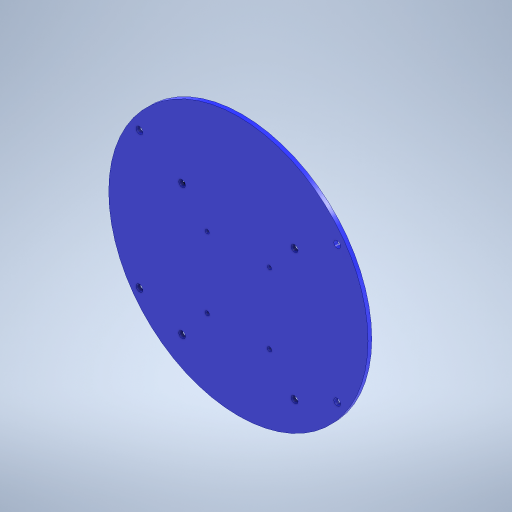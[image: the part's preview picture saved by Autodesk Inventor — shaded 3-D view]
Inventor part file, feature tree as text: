
AUTODESK INVENTOR PART (.ipt)
format: ipt  version: 2023 (Build 270158000, 158)  size: 334,848 bytes
history: native  units: mm
features: extrude x9, other x7, sketch x3, mirror x3, projected_geometry x1
ambient origin geometry x8: Origin, YZ Plane, XZ Plane, XY Plane, X Axis, Y Axis, Z Axis, Center Point
bodies: Body1 (feature_tree), Body2 (feature_tree), Body3 (feature_tree), Body4 (feature_tree), Body5 (feature_tree), Body6 (feature_tree), Body7 (feature_tree)
feature tree (23):
  other  "PCB_Azul"
  extrude  "Extrusión1"  Depth=1.6mm TaperAngle=0.0deg
  sketch  "Boceto2"  dims[d3=2.9mm d5=41.91mm]
  extrude  "Extrusión2"  Depth=41.91mm
  mirror  "Simetría1"
  mirror  "Simetría2"
  extrude  "Extrusión3"  Depth=12.5mm
  mirror  "Simetría3"
  sketch  "Boceto4"  dims[d6=23.875mm d8=12.5mm d9=1.6mm d10=0.0mm d11=1.6mm d12=0.0mm d13=55.5mm d14=1.85mm d15=30.0mm d16=1.7mm d17=13.21mm d18=29.5mm d19=51.1mm d20=5.0mm d21=2.15mm d22=13.35mm d23=0.0mm d24=25.2mm d25=5.11mm d26=5.86mm d27=15.0mm d28=2.5mm d29=33.5mm d30=10.15mm d31=8.4mm d32=43.0mm d33=24.5mm d34=9.8mm d35=4.35mm d36=26.25mm d37=7.5mm d38=12.75mm d39=7.75mm d40=14.5mm d41=6.5mm d42=4.3mm d43=0.0mm d44=4.5mm d45=0.0mm d46=0.85mm d47=0.0mm d48=2.45mm d49=0.0mm d50=6.25mm d51=10.0mm d52=20.0mm d53=5.75mm d54=0.0mm d55=26.04mm]
  extrude  "Extrusión4"  Depth=1.6mm TaperAngle=0.0deg
  extrude  "Extrusión5"  Depth=1.6mm TaperAngle=0.0deg
  extrude  "Extrusión6"  Depth=5.75mm
  extrude  "Extrusión7"  Depth=1.85mm
  extrude  "Extrusión8"  Depth=5.75mm
  extrude  "Extrusión9"  Depth=5.75mm
  sketch  "Boceto1"  dims[d0=110.0mm d1=1.6mm d2=0.0mm]
  projected_geometry  "Contorno proyectado1"
  other  "HAT_RPI"
  other  "Sólido3"
  other  "Sólido4"
  other  "Sólido5"
  other  "Sólido6"
  other  "Sólido7"
